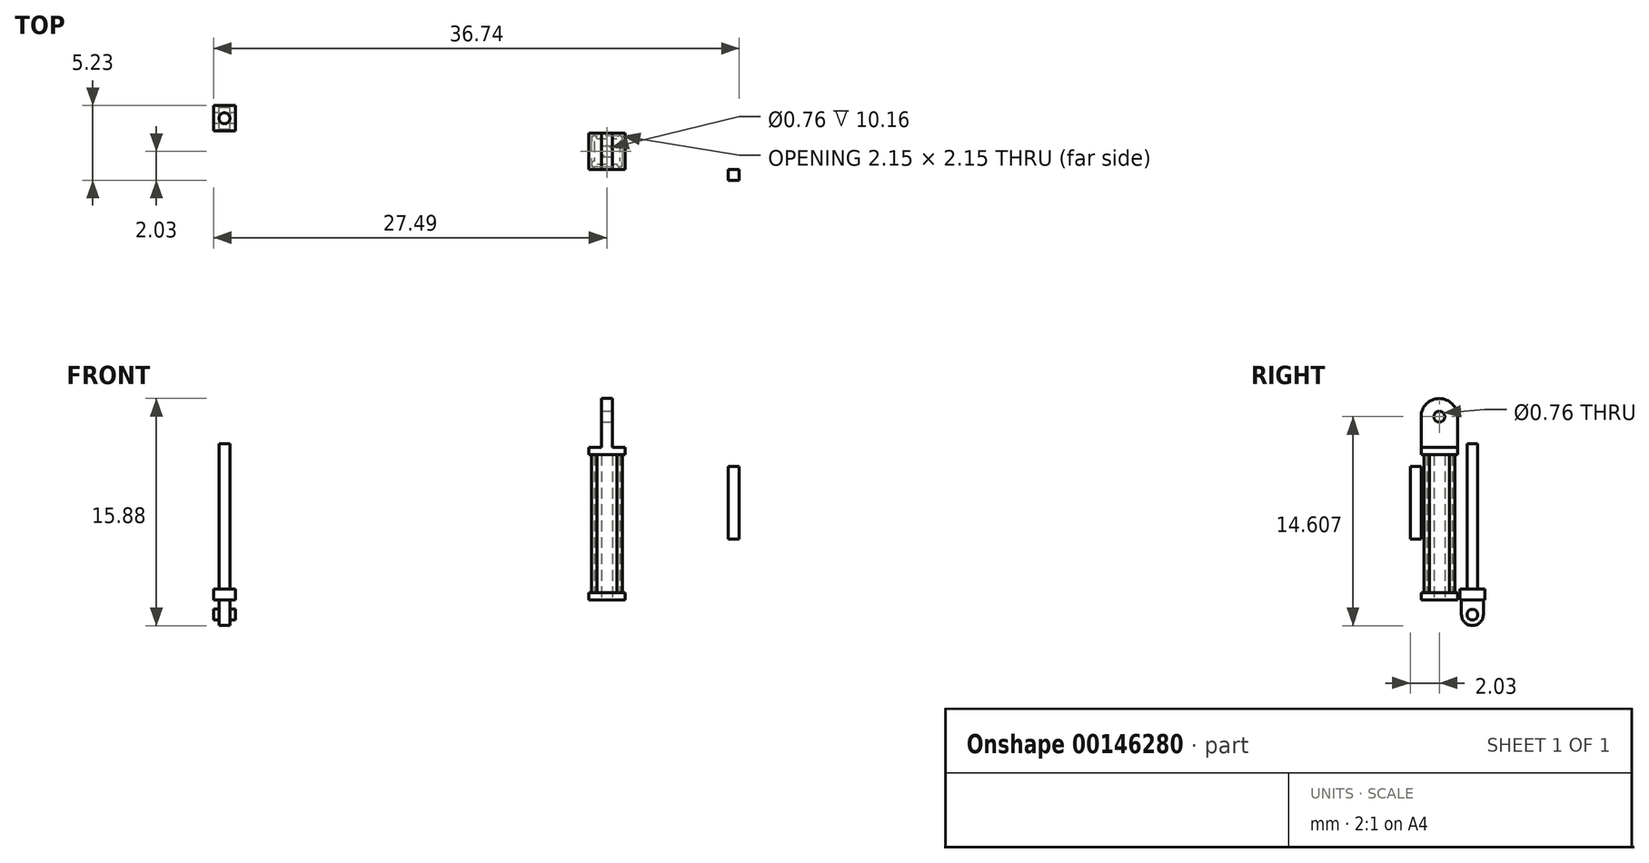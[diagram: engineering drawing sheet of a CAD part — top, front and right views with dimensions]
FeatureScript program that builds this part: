
annotation { "Feature Type Name" : "Feature", "Feature Type Description" : "" }
export const myFeature = defineFeature(function(context is Context, id is Id, definition is map)
    precondition{}
    {
        {
            var Q0;
            Q0=qCreatedBy(makeId("Top.planeOp"),FACE);
            var sketch = newSketch(context, id + "F0", { "sketchPlane" : qUnion([Q0])});
            skLineSegment(sketch, "E0.bottom", {"start": v(0, 0) * mm, "end": v(-2.54, 0) * mm});
            skLineSegment(sketch, "E0.top", {"start": v(0, 2.54) * mm, "end": v(-2.54, 2.54) * mm});
            skLineSegment(sketch, "E0.left", {"start": v(0, 0) * mm, "end": v(0, 2.54) * mm});
            skLineSegment(sketch, "E0.right", {"start": v(-2.54, 0) * mm, "end": v(-2.54, 2.54) * mm});
            skSolve(sketch);
        }
        {
            var Q0;
            Q0=makeQuery(id+"F0.imprint","IMPRINT",FACE,{"disambiguationData":[TD([[makeQuery(id+"F0.imprint","IMPRINT",EDGE,{"derivedFrom":sQuery(id+"F0.wireOp",EDGE,"E0.bottom")}),-1.0]])]});
            extrude(context, id + "F1", {"entities" : qUnion([Q0]), "depth" : 0.5 * mm});
        }
        {
            var Q0;
            Q0=makeQuery(id+"F1.opExtrude","CAP_FACE",FACE,{"disambiguationData":[OSD([sQuery(id+"F0.wireOp",EDGE,"E0.bottom"),sQuery(id+"F0.wireOp",EDGE,"E0.top"),sQuery(id+"F0.wireOp",EDGE,"E0.left"),sQuery(id+"F0.wireOp",EDGE,"E0.right")])],"isStart":false});
            var sketch = newSketch(context, id + "F2", { "sketchPlane" : qUnion([Q0])});
            skLineSegment(sketch, "E1.bottom", {"start": v(-2.16, 2.16) * mm, "end": v(-0.38, 2.16) * mm});
            skLineSegment(sketch, "E1.top", {"start": v(-2.16, 0.38) * mm, "end": v(-0.38, 0.38) * mm});
            skLineSegment(sketch, "E1.left", {"start": v(-2.16, 2.16) * mm, "end": v(-2.16, 0.38) * mm});
            skLineSegment(sketch, "E1.right", {"start": v(-0.38, 2.16) * mm, "end": v(-0.38, 0.38) * mm});
            skSolve(sketch);
        }
        {
            var Q0;
            Q0=makeQuery(id+"F1.opExtrude","CAP_FACE",FACE,{"disambiguationData":[OSD([sQuery(id+"F0.wireOp",EDGE,"E0.bottom"),sQuery(id+"F0.wireOp",EDGE,"E0.top"),sQuery(id+"F0.wireOp",EDGE,"E0.left"),sQuery(id+"F0.wireOp",EDGE,"E0.right")])],"isStart":false});
            var sketch = newSketch(context, id + "F3", { "sketchPlane" : qUnion([Q0])});
            skCircle(sketch, "E2", {"center": v(-2.16, 0.38) * mm, "radius": 0.2 * mm});
            skCircle(sketch, "E3", {"center": v(-0.38, 0.38) * mm, "radius": 0.2 * mm});
            skCircle(sketch, "E4", {"center": v(-0.38, 2.16) * mm, "radius": 0.2 * mm});
            skCircle(sketch, "E5", {"center": v(-2.16, 2.16) * mm, "radius": 0.2 * mm});
            skSolve(sketch);
        }
        {
            var Q0;
            Q0=qSketchRegion(id+"F3",true);
            var Q1;
            Q1=makeQuery(id+"F2.imprint","IMPRINT",FACE,{"disambiguationData":[TD([[makeQuery(id+"F2.imprint","IMPRINT",EDGE,{"derivedFrom":sQuery(id+"F2.wireOp",EDGE,"E1.bottom")}),-1.0]])]});
            extrude(context, id + "F4", {"entities" : qUnion([Q0, Q1]), "operationType" : NewBodyOperationType.ADD, "depth" : 9.65 * mm});
        }
        {
            var Q0;
            Q0=makeQuery(id+"F4.boolean.opBoolean","MERGE",FACE,{"derivedFrom":[makeQuery(id+"F4.opExtrude","CAP_FACE",FACE,{"disambiguationData":[OSD([sQuery(id+"F2.wireOp",EDGE,"E1.bottom"),sQuery(id+"F2.wireOp",EDGE,"E1.top"),sQuery(id+"F2.wireOp",EDGE,"E1.left"),sQuery(id+"F2.wireOp",EDGE,"E1.right")])],"isStart":false}),makeQuery(id+"F4.opExtrude","CAP_FACE",FACE,{"disambiguationData":[OSD([sQuery(id+"F3.wireOp",EDGE,"E2")])],"isStart":false}),makeQuery(id+"F4.opExtrude","CAP_FACE",FACE,{"disambiguationData":[OSD([sQuery(id+"F3.wireOp",EDGE,"E3")])],"isStart":false}),makeQuery(id+"F4.opExtrude","CAP_FACE",FACE,{"disambiguationData":[OSD([sQuery(id+"F3.wireOp",EDGE,"E4")])],"isStart":false}),makeQuery(id+"F4.opExtrude","CAP_FACE",FACE,{"disambiguationData":[OSD([sQuery(id+"F3.wireOp",EDGE,"E5")])],"isStart":false})]});
            var sketch = newSketch(context, id + "F5", { "sketchPlane" : qUnion([Q0])});
            skLineSegment(sketch, "E6.bottom", {"start": v(0, 0) * mm, "end": v(-2.54, 0) * mm});
            skLineSegment(sketch, "E6.top", {"start": v(0, 2.54) * mm, "end": v(-2.54, 2.54) * mm});
            skLineSegment(sketch, "E6.left", {"start": v(0, 0) * mm, "end": v(0, 2.54) * mm});
            skLineSegment(sketch, "E6.right", {"start": v(-2.54, 0) * mm, "end": v(-2.54, 2.54) * mm});
            skSolve(sketch);
        }
        {
            var Q0;
            Q0=qSketchRegion(id+"F5",true);
            extrude(context, id + "F6", {"entities" : qUnion([Q0]), "operationType" : NewBodyOperationType.ADD, "depth" : 0.5 * mm});
        }
        {
            var Q0;
            Q0=makeQuery(id+"F6.opExtrude","CAP_FACE",FACE,{"disambiguationData":[OSD([sQuery(id+"F5.wireOp",EDGE,"E6.bottom"),sQuery(id+"F5.wireOp",EDGE,"E6.top"),sQuery(id+"F5.wireOp",EDGE,"E6.left"),sQuery(id+"F5.wireOp",EDGE,"E6.right")])],"isStart":false});
            var sketch = newSketch(context, id + "F7", { "sketchPlane" : qUnion([Q0])});
            skLineSegment(sketch, "E7.bottom", {"start": v(-1.65, 2.54) * mm, "end": v(-0.89, 2.54) * mm});
            skLineSegment(sketch, "E7.top", {"start": v(-1.65, 0) * mm, "end": v(-0.89, 0) * mm});
            skLineSegment(sketch, "E7.left", {"start": v(-1.65, 2.54) * mm, "end": v(-1.65, 0) * mm});
            skLineSegment(sketch, "E7.right", {"start": v(-0.89, 2.54) * mm, "end": v(-0.89, 0) * mm});
            skSolve(sketch);
        }
        {
            var Q0;
            Q0=makeQuery(id+"F7.imprint","IMPRINT",FACE,{"disambiguationData":[TD([[makeQuery(id+"F7.imprint","IMPRINT",EDGE,{"derivedFrom":sQuery(id+"F7.wireOp",EDGE,"E7.bottom")}),-1.0]])]});
            var Q1;
            Q1=makeQuery(id+"F7.imprint","IMPRINT",FACE,{"disambiguationData":[TD([[makeQuery(id+"F7.imprint","IMPRINT",EDGE,{"derivedFrom":sQuery(id+"F7.wireOp",EDGE,"E7.bottom")}),1.0]])]});
            extrude(context, id + "F8", {"entities" : qUnion([Q0, Q1]), "operationType" : NewBodyOperationType.ADD, "depth" : 3.43 * mm});
        }
        {
            var Q0;
            Q0=makeQuery(id+"F8.opExtrude","CAP_EDGE",EDGE,{"disambiguationData":[OSD([sQuery(id+"F7.wireOp",EDGE,"SnMZz6UM-2eJR-UkkT-urh7-qXkrGxYPXZd4.bottom")])],"isStart":false});
            var Q1;
            Q1=makeQuery(id+"F8.opExtrude","CAP_EDGE",EDGE,{"disambiguationData":[OSD([sQuery(id+"F7.wireOp",EDGE,"SnMZz6UM-2eJR-UkkT-urh7-qXkrGxYPXZd4.top")])],"isStart":false});
            var Q2;
            Q2=makeQuery(id+"F8.opExtrude","CAP_EDGE",EDGE,{"disambiguationData":[OSD([sQuery(id+"F7.wireOp",EDGE,"E7.top")])],"isStart":false});
            var Q3;
            Q3=makeQuery(id+"F8.opExtrude","CAP_EDGE",EDGE,{"disambiguationData":[OSD([sQuery(id+"F7.wireOp",EDGE,"E7.bottom")])],"isStart":false});
            fillet(context, id + "F9", {"entities" : qUnion([Q0, Q1, Q2, Q3]), "radius" : 1.27 * mm, "tangentPropagation" : true, "allowEdgeOverflow" : false});
        }
        {
            var Q0;
            Q0=makeQuery(id+"F1.opExtrude","CAP_FACE",FACE,{"disambiguationData":[OSD([sQuery(id+"F0.wireOp",EDGE,"E0.bottom"),sQuery(id+"F0.wireOp",EDGE,"E0.top"),sQuery(id+"F0.wireOp",EDGE,"E0.left"),sQuery(id+"F0.wireOp",EDGE,"E0.right")])],"isStart":true});
            var sketch = newSketch(context, id + "F10", { "sketchPlane" : qUnion([Q0])});
            skCircle(sketch, "E8", {"center": v(-1.27, -1.27) * mm, "radius": 0.38 * mm});
            skPoint(sketch, "E8.centerSnap0", {"position": v(-1.27, -2.54) * mm});
            skPoint(sketch, "E8.centerSnap1", {"position": v(-2.54, -1.27) * mm});
            skSolve(sketch);
        }
        {
            var Q0;
            Q0=qSketchRegion(id+"F10",true);
            extrude(context, id + "F11", {"entities" : qUnion([Q0]), "operationType" : NewBodyOperationType.REMOVE, "oppositeDirection" : true, "depth" : 10.16 * mm});
        }
        {
            var Q0;
            Q0=qCreatedBy(makeId("Top.planeOp"),FACE);
            var sketch = newSketch(context, id + "F12", { "sketchPlane" : qUnion([Q0])});
            skLineSegment(sketch, "E9.bottom", {"start": v(-28.76, 4.47) * mm, "end": v(-27.24, 4.47) * mm});
            skLineSegment(sketch, "E9.top", {"start": v(-28.76, 2.7) * mm, "end": v(-27.24, 2.7) * mm});
            skLineSegment(sketch, "E9.left", {"start": v(-28.76, 4.47) * mm, "end": v(-28.76, 2.7) * mm});
            skLineSegment(sketch, "E9.right", {"start": v(-27.24, 4.47) * mm, "end": v(-27.24, 2.7) * mm});
            skSolve(sketch);
        }
        {
            var Q0;
            Q0=qSketchRegion(id+"F12",true);
            extrude(context, id + "F13", {"entities" : qUnion([Q0]), "depth" : 0.76 * mm});
        }
        {
            var Q0;
            Q0=makeQuery(id+"F13.opExtrude","CAP_FACE",FACE,{"disambiguationData":[OSD([sQuery(id+"F12.wireOp",EDGE,"E9.bottom"),sQuery(id+"F12.wireOp",EDGE,"E9.top"),sQuery(id+"F12.wireOp",EDGE,"E9.left"),sQuery(id+"F12.wireOp",EDGE,"E9.right")])],"isStart":false});
            var sketch = newSketch(context, id + "F14", { "sketchPlane" : qUnion([Q0])});
            skCircle(sketch, "E10", {"center": v(-28, 3.59) * mm, "radius": 0.38 * mm});
            skPoint(sketch, "E10.centerSnap0", {"position": v(-28.76, 3.59) * mm});
            skPoint(sketch, "E10.centerSnap1", {"position": v(-28, 4.47) * mm});
            skSolve(sketch);
        }
        {
            var Q0;
            Q0=qSketchRegion(id+"F14",true);
            extrude(context, id + "F15", {"entities" : qUnion([Q0]), "operationType" : NewBodyOperationType.ADD, "depth" : 10.16 * mm});
        }
        {
            var Q0;
            Q0=makeQuery(id+"F13.opExtrude","CAP_FACE",FACE,{"disambiguationData":[OSD([sQuery(id+"F12.wireOp",EDGE,"E9.bottom"),sQuery(id+"F12.wireOp",EDGE,"E9.top"),sQuery(id+"F12.wireOp",EDGE,"E9.left"),sQuery(id+"F12.wireOp",EDGE,"E9.right")])],"isStart":true});
            var sketch = newSketch(context, id + "F16", { "sketchPlane" : qUnion([Q0])});
            skLineSegment(sketch, "E11.bottom", {"start": v(-28.38, -2.82) * mm, "end": v(-27.62, -2.82) * mm});
            skLineSegment(sketch, "E11.top", {"start": v(-28.38, -4.35) * mm, "end": v(-27.62, -4.35) * mm});
            skLineSegment(sketch, "E11.left", {"start": v(-28.38, -2.82) * mm, "end": v(-28.38, -4.35) * mm});
            skLineSegment(sketch, "E11.right", {"start": v(-27.62, -2.82) * mm, "end": v(-27.62, -4.35) * mm});
            skSolve(sketch);
        }
        {
            var Q0;
            Q0=qSketchRegion(id+"F16",true);
            extrude(context, id + "F17", {"entities" : qUnion([Q0]), "operationType" : NewBodyOperationType.ADD, "depth" : 1.78 * mm});
        }
        {
            var Q0;
            Q0=makeQuery(id+"F17.opExtrude","CAP_EDGE",EDGE,{"disambiguationData":[OSD([sQuery(id+"F16.wireOp",EDGE,"E11.bottom")])],"isStart":false});
            var Q1;
            Q1=makeQuery(id+"F17.opExtrude","CAP_EDGE",EDGE,{"disambiguationData":[OSD([sQuery(id+"F16.wireOp",EDGE,"E11.top")])],"isStart":false});
            var Q2;
            Q2=makeQuery(id+"F17.opExtrude","CAP_EDGE",EDGE,{"disambiguationData":[OSD([sQuery(id+"F16.wireOp",EDGE,"ZLugjXCQ-A49h-u4Kn-CDT1-VXdTF1MAhCxP.top")])],"isStart":false});
            var Q3;
            Q3=makeQuery(id+"F17.opExtrude","CAP_EDGE",EDGE,{"disambiguationData":[OSD([sQuery(id+"F16.wireOp",EDGE,"ZLugjXCQ-A49h-u4Kn-CDT1-VXdTF1MAhCxP.bottom")])],"isStart":false});
            fillet(context, id + "F18", {"entities" : qUnion([Q0, Q1, Q2, Q3]), "radius" : 0.76 * mm, "tangentPropagation" : true, "allowEdgeOverflow" : false});
        }
        {
            var Q0;
            Q0=makeQuery(id+"F8.opExtrude","SWEPT_FACE",FACE,{"disambiguationData":[OSD([sQuery(id+"F7.wireOp",EDGE,"E7.right")])]});
            var sketch = newSketch(context, id + "F19", { "sketchPlane" : qUnion([Q0])});
            skCircle(sketch, "E12", {"center": v(1.27, 12.83) * mm, "radius": 0.38 * mm});
            skSolve(sketch);
        }
        {
            var Q0;
            Q0=makeQuery(id+"F17.opExtrude","SWEPT_FACE",FACE,{"disambiguationData":[OSD([sQuery(id+"F16.wireOp",EDGE,"E11.right")])]});
            var sketch = newSketch(context, id + "F20", { "sketchPlane" : qUnion([Q0])});
            skCircle(sketch, "E13", {"center": v(3.59, -1.02) * mm, "radius": 0.38 * mm});
            skSolve(sketch);
        }
        {
            var Q0;
            Q0=qSketchRegion(id+"F20",true);
            extrude(context, id + "F21", {"entities" : qUnion([Q0]), "operationType" : NewBodyOperationType.ADD, "depth" : 0.38 * mm, "hasSecondDirection" : true, "secondDirectionOppositeDirection" : true, "secondDirectionDepth" : 1.14 * mm});
        }
        {
            var Q0;
            Q0 = qSketchRegion(id + "F19", true);
            extrude(context, id + "F22", {"entities" : qUnion([Q0]), "operationType" : NewBodyOperationType.REMOVE, "oppositeDirection" : true, "depth" : 0.76 * mm});
        }
        {
            var Q0;
            Q0=qCreatedBy(makeId("Front.planeOp"),FACE);
            var sketch = newSketch(context, id + "F23", { "sketchPlane" : qUnion([Q0])});
            skLineSegment(sketch, "E14.bottom", {"start": v(7.22, 9.34) * mm, "end": v(7.98, 9.34) * mm});
            skLineSegment(sketch, "E14.top", {"start": v(7.22, 4.26) * mm, "end": v(7.98, 4.26) * mm});
            skLineSegment(sketch, "E14.left", {"start": v(7.22, 9.34) * mm, "end": v(7.22, 4.26) * mm});
            skLineSegment(sketch, "E14.right", {"start": v(7.98, 9.34) * mm, "end": v(7.98, 4.26) * mm});
            skSolve(sketch);
        }
        {
            var Q0;
            Q0 = qSketchRegion(id + "F23", true);
            extrude(context, id + "F24", {"entities" : qUnion([Q0]), "flatOperationType" : FlatOperationType.REMOVE, "offsetDistance" : 25.4 * mm, "depth" : 0.76 * mm, "domain" : OperationDomain.MODEL});
        }
    });
